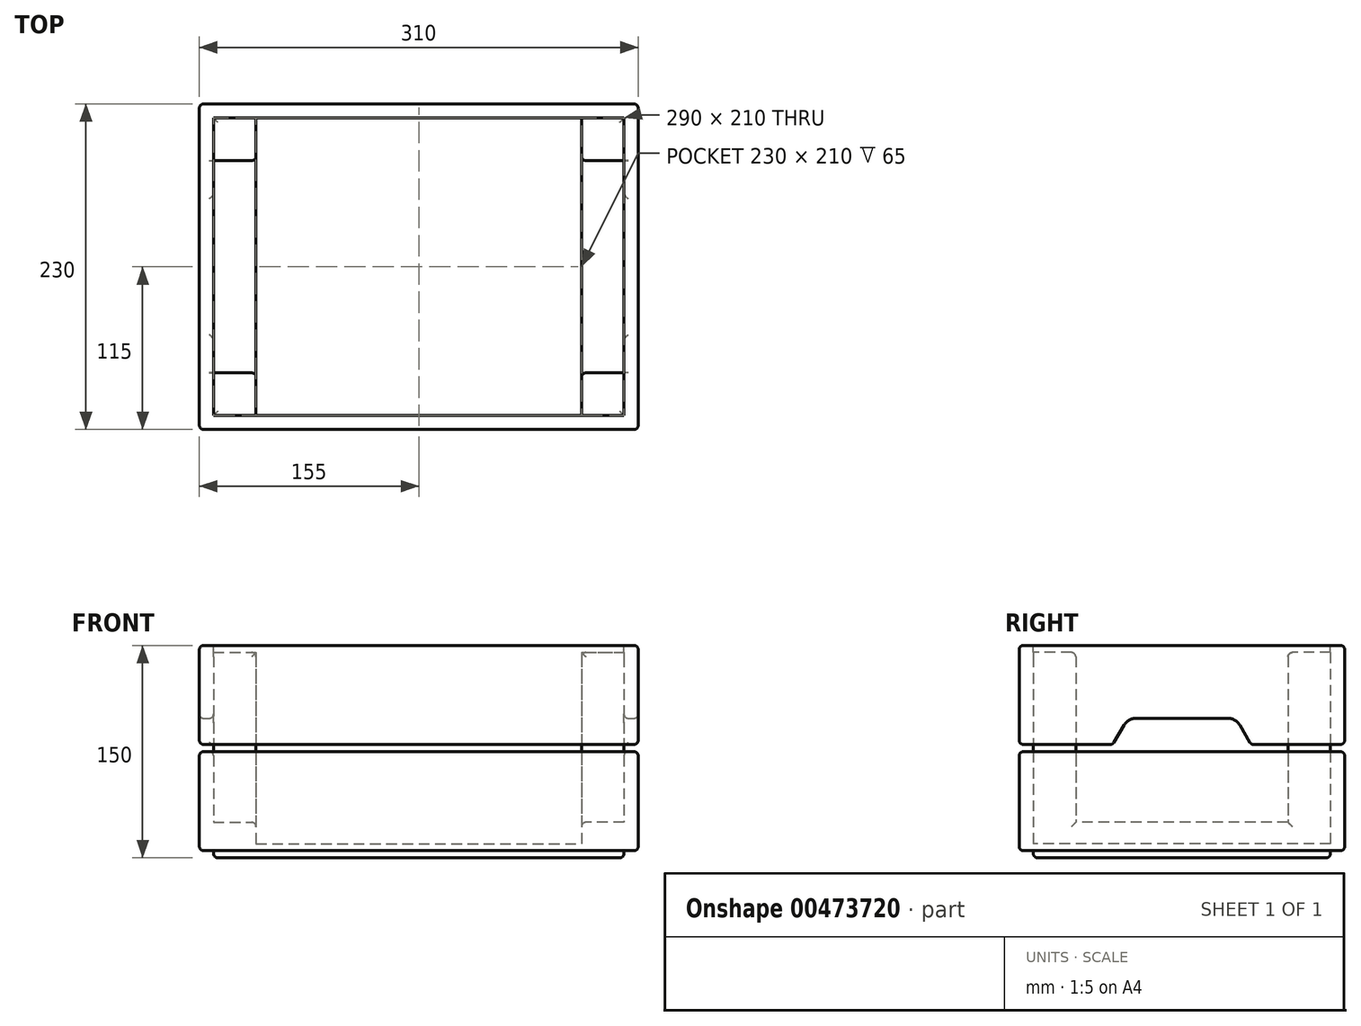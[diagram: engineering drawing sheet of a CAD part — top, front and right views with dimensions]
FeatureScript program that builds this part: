
annotation { "Feature Type Name" : "Feature", "Feature Type Description" : "" }
export const myFeature = defineFeature(function(context is Context, id is Id, definition is map)
    precondition{}
    {
        {
            var Q0;
            Q0=qCreatedBy(makeId("Top.planeOp"),FACE);
            var sketch = newSketch(context, id + "F0", { "sketchPlane" : qUnion([Q0])});
            skLineSegment(sketch, "E0.bottom", {"start": v(-155, 115) * mm, "end": v(155, 115) * mm});
            skLineSegment(sketch, "E0.top", {"start": v(-155, -115) * mm, "end": v(155, -115) * mm});
            skLineSegment(sketch, "E0.left", {"start": v(-155, 115) * mm, "end": v(-155, -115) * mm});
            skLineSegment(sketch, "E0.right", {"start": v(155, 115) * mm, "end": v(155, -115) * mm});
            skSolve(sketch);
        }
        {
            var Q0;
            Q0=makeQuery(id+"F0.imprint","IMPRINT",FACE,{"disambiguationData":[TD([[makeQuery(id+"F0.imprint","IMPRINT",EDGE,{"derivedFrom":sQuery(id+"F0.wireOp",EDGE,"E0.bottom")}),-1.0]])]});
            var sketch = newSketch(context, id + "F1", { "sketchPlane" : qUnion([Q0])});
            skLineSegment(sketch, "E1.0", {"start": v(-145, 105) * mm, "end": v(145, 105) * mm});
            skLineSegment(sketch, "E1.1", {"start": v(-145, 105) * mm, "end": v(-145, -105) * mm});
            skLineSegment(sketch, "E1.2", {"start": v(-145, -105) * mm, "end": v(145, -105) * mm});
            skLineSegment(sketch, "E1.3", {"start": v(145, 105) * mm, "end": v(145, -105) * mm});
            skSolve(sketch);
        }
        {
            var Q0;
            Q0=makeQuery(id+"F0.imprint","IMPRINT",FACE,{"disambiguationData":[TD([[makeQuery(id+"F0.imprint","IMPRINT",EDGE,{"derivedFrom":sQuery(id+"F0.wireOp",EDGE,"E0.bottom")}),-1.0]])]});
            extrude(context, id + "F2", {"entities" : qUnion([Q0]), "depth" : 145 * mm});
        }
        {
            var Q0;
            Q0=makeQuery(id+"F1.imprint","IMPRINT",FACE,{"disambiguationData":[TD([[makeQuery(id+"F1.imprint","IMPRINT",EDGE,{"derivedFrom":sQuery(id+"F1.wireOp",EDGE,"E1.0")}),-1.0]])]});
            extrude(context, id + "F3", {"entities" : qUnion([Q0]), "operationType" : NewBodyOperationType.ADD, "oppositeDirection" : true, "depth" : 5 * mm});
        }
        {
            var Q0;
            Q0=makeQuery(id+"F2.opExtrude","CAP_FACE",FACE,{"disambiguationData":[OSD([sQuery(id+"F0.wireOp",EDGE,"E0.bottom"),sQuery(id+"F0.wireOp",EDGE,"E0.top"),sQuery(id+"F0.wireOp",EDGE,"E0.left"),sQuery(id+"F0.wireOp",EDGE,"E0.right")])],"isStart":false});
            var sketch = newSketch(context, id + "F4", { "sketchPlane" : qUnion([Q0])});
            skLineSegment(sketch, "E2.0", {"start": v(-145, 105) * mm, "end": v(145, 105) * mm});
            skLineSegment(sketch, "E2.1", {"start": v(-145, 105) * mm, "end": v(-145, -105) * mm});
            skLineSegment(sketch, "E2.2", {"start": v(-145, -105) * mm, "end": v(145, -105) * mm});
            skLineSegment(sketch, "E2.3", {"start": v(145, 105) * mm, "end": v(145, -105) * mm});
            skSolve(sketch);
        }
        {
            var Q0;
            Q0=makeQuery(id+"F4.imprint","IMPRINT",FACE,{"disambiguationData":[TD([[makeQuery(id+"F4.imprint","IMPRINT",EDGE,{"derivedFrom":sQuery(id+"F4.wireOp",EDGE,"E2.0")}),-1.0]])]});
            extrude(context, id + "F5", {"entities" : qUnion([Q0]), "operationType" : NewBodyOperationType.REMOVE, "oppositeDirection" : true, "depth" : 140 * mm});
        }
        {
            var Q0;
            Q0=makeQuery(id+"F2.opExtrude","SWEPT_FACE",FACE,{"disambiguationData":[OSD([sQuery(id+"F0.wireOp",EDGE,"E0.right")])]});
            var sketch = newSketch(context, id + "F6", { "sketchPlane" : qUnion([Q0])});
            skLineSegment(sketch, "E3.bottom", {"start": v(-115, 145) * mm, "end": v(115, 145) * mm});
            skLineSegment(sketch, "E3.top", {"start": v(-115, 75) * mm, "end": v(-49, 75) * mm});
            skLineSegment(sketch, "E3.left", {"start": v(-115, 145) * mm, "end": v(-115, 75) * mm});
            skLineSegment(sketch, "E3.right", {"start": v(115, 145) * mm, "end": v(115, 75) * mm});
            skLineSegment(sketch, "E4.bottom", {"start": v(-115, 0) * mm, "end": v(115, 0) * mm});
            skLineSegment(sketch, "E4.top", {"start": v(-115, 70) * mm, "end": v(115, 70) * mm});
            skLineSegment(sketch, "E4.left", {"start": v(-115, 0) * mm, "end": v(-115, 70) * mm});
            skLineSegment(sketch, "E4.right", {"start": v(115, 0) * mm, "end": v(115, 70) * mm});
            skLineSegment(sketch, "E5", {"start": v(-115, 93.5) * mm, "end": v(115, 93.5) * mm, "construction": true});
            skLineSegment(sketch, "E6", {"start": v(49, 145) * mm, "end": v(49, 75) * mm, "construction": true});
            skLineSegment(sketch, "E7", {"start": v(-49, 145) * mm, "end": v(-49, 75) * mm, "construction": true});
            skLineSegment(sketch, "E8", {"start": v(-38, 145) * mm, "end": v(-38, 75) * mm, "construction": true});
            skLineSegment(sketch, "E9", {"start": v(38, 145) * mm, "end": v(38, 75) * mm, "construction": true});
            skLineSegment(sketch, "E10", {"start": v(-49, 75) * mm, "end": v(-40.9, 88.61) * mm});
            skLineSegment(sketch, "E11", {"start": v(-32.31, 93.5) * mm, "end": v(32.31, 93.5) * mm});
            skLineSegment(sketch, "E12", {"start": v(40.9, 88.61) * mm, "end": v(49, 75) * mm});
            skLineSegment(sketch, "E13.trimOffspring", {"start": v(49, 75) * mm, "end": v(115, 75) * mm});
            skPoint(sketch, "E14.visualSharp", {"position": v(-38, 93.5) * mm});
            skArc(sketch, "E14.filletArc", {"start": v(-32.31, 93.5) * mm, "mid": v(-37.26, 92.2) * mm, "end": v(-40.9, 88.61) * mm});
            skPoint(sketch, "E15.visualSharp", {"position": v(38, 93.5) * mm});
            skArc(sketch, "E15.filletArc", {"start": v(40.9, 88.61) * mm, "mid": v(37.26, 92.2) * mm, "end": v(32.31, 93.5) * mm});
            skLineSegment(sketch, "E16", {"start": v(-115, 75) * mm, "end": v(-115, 70) * mm});
            skLineSegment(sketch, "E17", {"start": v(115, 75) * mm, "end": v(115, 70) * mm});
            skSolve(sketch);
        }
        {
            var Q0;
            Q0=makeQuery(id+"F6.imprint","IMPRINT",FACE,{"disambiguationData":[TD([[makeQuery(id+"F6.imprint","IMPRINT",EDGE,{"derivedFrom":sQuery(id+"F6.wireOp",EDGE,"E3.top")}),-1.0]])]});
            extrude(context, id + "F7", {"entities" : qUnion([Q0]), "operationType" : NewBodyOperationType.REMOVE, "endBound" : BoundingType.THROUGH_ALL, "oppositeDirection" : true, "depth" : 25 * mm});
        }
        {
            var Q0;
            Q0=makeQuery(id+"F5.boolean.opBoolean","COPY",FACE,{"derivedFrom":makeQuery(id+"F5.opExtrude","CAP_FACE",FACE,{"disambiguationData":[OSD([sQuery(id+"F4.wireOp",EDGE,"E2.0"),sQuery(id+"F4.wireOp",EDGE,"E2.1"),sQuery(id+"F4.wireOp",EDGE,"E2.2"),sQuery(id+"F4.wireOp",EDGE,"E2.3")])],"isStart":false})});
            var sketch = newSketch(context, id + "F8", { "sketchPlane" : qUnion([Q0])});
            skLineSegment(sketch, "E18.bottom", {"start": v(-145, 105) * mm, "end": v(-115, 105) * mm});
            skLineSegment(sketch, "E18.top", {"start": v(-145, 75) * mm, "end": v(-115, 75) * mm});
            skLineSegment(sketch, "E18.left", {"start": v(-145, 105) * mm, "end": v(-145, 75) * mm});
            skLineSegment(sketch, "E18.right", {"start": v(-115, 105) * mm, "end": v(-115, 75) * mm});
            skLineSegment(sketch, "E19.MirrorCS", {"start": v(-145, -75) * mm, "end": v(-115, -75) * mm});
            skLineSegment(sketch, "E20.MirrorCS", {"start": v(-145, -105) * mm, "end": v(-145, -75) * mm});
            skLineSegment(sketch, "E21.MirrorCS", {"start": v(-145, -105) * mm, "end": v(-115, -105) * mm});
            skLineSegment(sketch, "E22.MirrorCS", {"start": v(-115, -105) * mm, "end": v(-115, -75) * mm});
            skLineSegment(sketch, "E23.MirrorCS", {"start": v(145, 75) * mm, "end": v(115, 75) * mm});
            skLineSegment(sketch, "E24.MirrorCS", {"start": v(145, 105) * mm, "end": v(145, 75) * mm});
            skLineSegment(sketch, "E25.MirrorCS", {"start": v(145, 105) * mm, "end": v(115, 105) * mm});
            skLineSegment(sketch, "E26.MirrorCS", {"start": v(115, 105) * mm, "end": v(115, 75) * mm});
            skLineSegment(sketch, "E27.MirrorCS", {"start": v(145, -75) * mm, "end": v(115, -75) * mm});
            skLineSegment(sketch, "E28.MirrorCS", {"start": v(145, -105) * mm, "end": v(145, -75) * mm});
            skLineSegment(sketch, "E29.MirrorCS", {"start": v(145, -105) * mm, "end": v(115, -105) * mm});
            skLineSegment(sketch, "E30.MirrorCS", {"start": v(115, -105) * mm, "end": v(115, -75) * mm});
            skSolve(sketch);
        }
        {
            var Q0;
            Q0=makeQuery(id+"F8.imprint","IMPRINT",FACE,{"disambiguationData":[TD([[makeQuery(id+"F8.imprint","IMPRINT",EDGE,{"derivedFrom":sQuery(id+"F8.wireOp",EDGE,"E18.bottom")}),-1.0]])]});
            var Q1;
            Q1=makeQuery(id+"F8.imprint","IMPRINT",FACE,{"disambiguationData":[TD([[makeQuery(id+"F8.imprint","IMPRINT",EDGE,{"derivedFrom":sQuery(id+"F8.wireOp",EDGE,"E23.MirrorCS")}),-1.0]])]});
            var Q2;
            Q2=makeQuery(id+"F8.imprint","IMPRINT",FACE,{"disambiguationData":[TD([[makeQuery(id+"F8.imprint","IMPRINT",EDGE,{"derivedFrom":sQuery(id+"F8.wireOp",EDGE,"E27.MirrorCS")}),1.0]])]});
            var Q3;
            Q3=makeQuery(id+"F8.imprint","IMPRINT",FACE,{"disambiguationData":[TD([[makeQuery(id+"F8.imprint","IMPRINT",EDGE,{"derivedFrom":sQuery(id+"F8.wireOp",EDGE,"E19.MirrorCS")}),-1.0]])]});
            var Q4;
            Q4=makeQuery(id+"F2.opExtrude","CAP_FACE",FACE,{"disambiguationData":[OSD([sQuery(id+"F0.wireOp",EDGE,"E0.bottom"),sQuery(id+"F0.wireOp",EDGE,"E0.top"),sQuery(id+"F0.wireOp",EDGE,"E0.left"),sQuery(id+"F0.wireOp",EDGE,"E0.right")])],"isStart":false});
            extrude(context, id + "F9", {"entities" : qUnion([Q0, Q1, Q2, Q3]), "operationType" : NewBodyOperationType.ADD, "endBoundEntityFace" : qUnion([Q4]), "depth" : 135 * mm, "hasSecondDirection" : true, "secondDirectionOppositeDirection" : false, "secondDirectionDepth" : 15 * mm});
        }
        {
            var Q0;
            Q0=makeQuery(id+"F5.boolean.opBoolean","COPY",FACE,{"derivedFrom":makeQuery(id+"F5.opExtrude","CAP_FACE",FACE,{"disambiguationData":[OSD([sQuery(id+"F4.wireOp",EDGE,"E2.0"),sQuery(id+"F4.wireOp",EDGE,"E2.1"),sQuery(id+"F4.wireOp",EDGE,"E2.2"),sQuery(id+"F4.wireOp",EDGE,"E2.3")])],"isStart":false})});
            var sketch = newSketch(context, id + "F10", { "sketchPlane" : qUnion([Q0])});
            skLineSegment(sketch, "E31.0", {"start": v(115, -105) * mm, "end": v(115, -75) * mm});
            skLineSegment(sketch, "E32.bottom", {"start": v(145, 105) * mm, "end": v(115, 105) * mm});
            skLineSegment(sketch, "E32.top", {"start": v(145, -105) * mm, "end": v(115, -105) * mm});
            skLineSegment(sketch, "E32.left", {"start": v(145, 105) * mm, "end": v(145, -105) * mm});
            skLineSegment(sketch, "E32.right", {"start": v(115, 105) * mm, "end": v(115, -105) * mm});
            skLineSegment(sketch, "E33.MirrorCS", {"start": v(-115, 105) * mm, "end": v(-115, -105) * mm});
            skLineSegment(sketch, "E34.MirrorCS", {"start": v(-145, -105) * mm, "end": v(-115, -105) * mm});
            skLineSegment(sketch, "E35.MirrorCS", {"start": v(-145, 105) * mm, "end": v(-145, -105) * mm});
            skLineSegment(sketch, "E36.MirrorCS", {"start": v(-145, 105) * mm, "end": v(-115, 105) * mm});
            skSolve(sketch);
        }
        {
            var Q0;
            {var subQ1=sQuery(id+"F10.wireOp",EDGE,"E32.bottom");Q0=makeQuery(id+"F10.imprint","IMPRINT",FACE,{"disambiguationData":[TD([[makeQuery(id+"F10.imprint","IMPRINT",EDGE,{"derivedFrom":subQ1}),-1.0]])]});}
            var Q1;
            Q1=makeQuery(id+"F10.imprint","IMPRINT",FACE,{"disambiguationData":[TD([[makeQuery(id+"F10.imprint","IMPRINT",EDGE,{"derivedFrom":sQuery(id+"F10.wireOp",EDGE,"E33.MirrorCS")}),-1.0]])]});
            extrude(context, id + "F11", {"entities" : qUnion([Q0, Q1]), "operationType" : NewBodyOperationType.ADD, "depth" : 15 * mm});
        }
        {
            var Q0;
            {var subQ1=sQuery(id+"F0.wireOp",EDGE,"E0.right");Q0=makeQuery(id+"F7.boolean.opBoolean","SPLIT",FACE,{"disambiguationData":[TD([makeQuery(id+"F7.opExtrude","SWEPT_FACE",FACE,{"disambiguationData":[OSD([sQuery(id+"F6.wireOp",EDGE,"E4.top")])]})])],"derivedFrom":makeQuery(id+"F2.opExtrude","SWEPT_FACE",FACE,{"disambiguationData":[OSD([subQ1])]})});}
            var Q1;
            {var subQ1=sQuery(id+"F0.wireOp",EDGE,"E0.right");Q1=makeQuery(id+"F7.boolean.opBoolean","SPLIT",FACE,{"disambiguationData":[TD([makeQuery(id+"F7.opExtrude","SWEPT_FACE",FACE,{"disambiguationData":[OSD([sQuery(id+"F6.wireOp",EDGE,"E3.top")])]})])],"derivedFrom":makeQuery(id+"F2.opExtrude","SWEPT_FACE",FACE,{"disambiguationData":[OSD([subQ1])]})});}
            var Q2;
            {var subQ2=sQuery(id+"F0.wireOp",EDGE,"E0.top");Q2=makeQuery(id+"F7.boolean.opBoolean","SPLIT",FACE,{"disambiguationData":[TD([makeQuery(id+"F7.opExtrude","SWEPT_FACE",FACE,{"disambiguationData":[OSD([sQuery(id+"F6.wireOp",EDGE,"E4.top")])]})])],"derivedFrom":makeQuery(id+"F2.opExtrude","SWEPT_FACE",FACE,{"disambiguationData":[OSD([subQ2])]})});}
            var Q3;
            {var subQ2=sQuery(id+"F0.wireOp",EDGE,"E0.top");Q3=makeQuery(id+"F7.boolean.opBoolean","SPLIT",FACE,{"disambiguationData":[TD([makeQuery(id+"F7.opExtrude","SWEPT_FACE",FACE,{"disambiguationData":[OSD([sQuery(id+"F6.wireOp",EDGE,"E3.top")])]})])],"derivedFrom":makeQuery(id+"F2.opExtrude","SWEPT_FACE",FACE,{"disambiguationData":[OSD([subQ2])]})});}
            var Q4;
            {var subQ1=sQuery(id+"F0.wireOp",EDGE,"E0.left");Q4=makeQuery(id+"F7.boolean.opBoolean","SPLIT",FACE,{"disambiguationData":[TD([makeQuery(id+"F7.opExtrude","SWEPT_FACE",FACE,{"disambiguationData":[OSD([sQuery(id+"F6.wireOp",EDGE,"E3.top")])]})])],"derivedFrom":makeQuery(id+"F2.opExtrude","SWEPT_FACE",FACE,{"disambiguationData":[OSD([subQ1])]})});}
            var Q5;
            {var subQ1=sQuery(id+"F0.wireOp",EDGE,"E0.left");Q5=makeQuery(id+"F7.boolean.opBoolean","SPLIT",FACE,{"disambiguationData":[TD([makeQuery(id+"F7.opExtrude","SWEPT_FACE",FACE,{"disambiguationData":[OSD([sQuery(id+"F6.wireOp",EDGE,"E4.top")])]})])],"derivedFrom":makeQuery(id+"F2.opExtrude","SWEPT_FACE",FACE,{"disambiguationData":[OSD([subQ1])]})});}
            var Q6;
            {var subQ2=sQuery(id+"F0.wireOp",EDGE,"E0.bottom");Q6=makeQuery(id+"F7.boolean.opBoolean","SPLIT",FACE,{"disambiguationData":[TD([makeQuery(id+"F7.opExtrude","SWEPT_FACE",FACE,{"disambiguationData":[OSD([sQuery(id+"F6.wireOp",EDGE,"E4.top")])]})])],"derivedFrom":makeQuery(id+"F2.opExtrude","SWEPT_FACE",FACE,{"disambiguationData":[OSD([subQ2])]})});}
            var Q7;
            {var subQ2=sQuery(id+"F0.wireOp",EDGE,"E0.bottom");Q7=makeQuery(id+"F7.boolean.opBoolean","SPLIT",FACE,{"disambiguationData":[TD([makeQuery(id+"F7.opExtrude","SWEPT_FACE",FACE,{"disambiguationData":[OSD([sQuery(id+"F6.wireOp",EDGE,"E13.trimOffspring")])]})])],"derivedFrom":makeQuery(id+"F2.opExtrude","SWEPT_FACE",FACE,{"disambiguationData":[OSD([subQ2])]})});}
            var Q8;
            Q8=makeQuery(id+"F5.boolean.opBoolean","COPY",EDGE,{"derivedFrom":makeQuery(id+"F5.opExtrude","CAP_EDGE",EDGE,{"disambiguationData":[OSD([sQuery(id+"F4.wireOp",EDGE,"E2.0")])],"isStart":true})});
            var Q9;
            Q9=makeQuery(id+"F5.boolean.opBoolean","COPY",EDGE,{"derivedFrom":makeQuery(id+"F5.opExtrude","CAP_EDGE",EDGE,{"disambiguationData":[OSD([sQuery(id+"F4.wireOp",EDGE,"E2.3")])],"isStart":true})});
            var Q10;
            Q10=makeQuery(id+"F5.boolean.opBoolean","COPY",EDGE,{"derivedFrom":makeQuery(id+"F5.opExtrude","CAP_EDGE",EDGE,{"disambiguationData":[OSD([sQuery(id+"F4.wireOp",EDGE,"E2.2")])],"isStart":true})});
            var Q11;
            Q11=makeQuery(id+"F5.boolean.opBoolean","COPY",EDGE,{"derivedFrom":makeQuery(id+"F5.opExtrude","CAP_EDGE",EDGE,{"disambiguationData":[OSD([sQuery(id+"F4.wireOp",EDGE,"E2.1")])],"isStart":true})});
            var Q12;
            Q12=makeQuery(id+"F9.opExtrude","CAP_EDGE",EDGE,{"disambiguationData":[OSD([sQuery(id+"F8.wireOp",EDGE,"E19.MirrorCS")])],"isStart":false});
            var Q13;
            Q13=makeQuery(id+"F9.opExtrude","CAP_EDGE",EDGE,{"disambiguationData":[OSD([sQuery(id+"F8.wireOp",EDGE,"E22.MirrorCS")])],"isStart":false});
            var Q14;
            Q14=makeQuery(id+"F9.opExtrude","SWEPT_EDGE",EDGE,{"disambiguationData":[OSD([sQuery(id+"F8.wireOp",EDGE,"E19.MirrorCS"),sQuery(id+"F8.wireOp",EDGE,"E22.MirrorCS")])]});
            var Q15;
            Q15=makeQuery(id+"F9.opExtrude","CAP_EDGE",EDGE,{"disambiguationData":[OSD([sQuery(id+"F8.wireOp",EDGE,"E30.MirrorCS")])],"isStart":false});
            var Q16;
            Q16=makeQuery(id+"F9.opExtrude","SWEPT_EDGE",EDGE,{"disambiguationData":[OSD([sQuery(id+"F8.wireOp",EDGE,"E27.MirrorCS"),sQuery(id+"F8.wireOp",EDGE,"E30.MirrorCS")])]});
            var Q17;
            Q17=makeQuery(id+"F9.opExtrude","CAP_EDGE",EDGE,{"disambiguationData":[OSD([sQuery(id+"F8.wireOp",EDGE,"E27.MirrorCS")])],"isStart":false});
            var Q18;
            Q18=makeQuery(id+"F11.opExtrude","CAP_EDGE",EDGE,{"disambiguationData":[OSD([sQuery(id+"F10.wireOp",EDGE,"E32.right")])],"isStart":false});
            var Q19;
            Q19=makeQuery(id+"F9.opExtrude","SWEPT_EDGE",EDGE,{"disambiguationData":[OSD([sQuery(id+"F8.wireOp",EDGE,"E23.MirrorCS"),sQuery(id+"F8.wireOp",EDGE,"E26.MirrorCS")])]});
            var Q20;
            Q20=makeQuery(id+"F9.opExtrude","CAP_EDGE",EDGE,{"disambiguationData":[OSD([sQuery(id+"F8.wireOp",EDGE,"E23.MirrorCS")])],"isStart":false});
            var Q21;
            Q21=makeQuery(id+"F11.opExtrude","CAP_EDGE",EDGE,{"disambiguationData":[OSD([sQuery(id+"F10.wireOp",EDGE,"E33.MirrorCS")])],"isStart":false});
            var Q22;
            Q22=makeQuery(id+"F9.opExtrude","SWEPT_EDGE",EDGE,{"disambiguationData":[OSD([sQuery(id+"F8.wireOp",EDGE,"E18.top"),sQuery(id+"F8.wireOp",EDGE,"E18.right")])]});
            var Q23;
            Q23=makeQuery(id+"F9.opExtrude","CAP_EDGE",EDGE,{"disambiguationData":[OSD([sQuery(id+"F8.wireOp",EDGE,"E18.top")])],"isStart":false});
            var Q24;
            {var subQ0=makeQuery(id+"F5.boolean.opBoolean","COPY",FACE,{"derivedFrom":makeQuery(id+"F5.opExtrude","SWEPT_FACE",FACE,{"disambiguationData":[OSD([sQuery(id+"F4.wireOp",EDGE,"E2.3")])]})});var subQ1=makeQuery(id+"F7.opExtrude","SWEPT_FACE",FACE,{"disambiguationData":[OSD([sQuery(id+"F6.wireOp",EDGE,"E4.top")])]});Q24=makeQuery(id+"F9.boolean.opBoolean","SPLIT",EDGE,{"disambiguationData":[topologyDisambiguationEdgeConnected([subQ0])],"derivedFrom":makeQuery(id+"F7.boolean.opBoolean","INTERSECT",EDGE,{"derivedFrom":[subQ0,subQ1]})});}
            var Q25;
            {var subQ0=makeQuery(id+"F5.boolean.opBoolean","COPY",FACE,{"derivedFrom":makeQuery(id+"F5.opExtrude","SWEPT_FACE",FACE,{"disambiguationData":[OSD([sQuery(id+"F4.wireOp",EDGE,"E2.1")])]})});var subQ1=makeQuery(id+"F7.opExtrude","SWEPT_FACE",FACE,{"disambiguationData":[OSD([sQuery(id+"F6.wireOp",EDGE,"E4.top")])]});Q25=makeQuery(id+"F9.boolean.opBoolean","SPLIT",EDGE,{"disambiguationData":[topologyDisambiguationEdgeConnected([subQ0])],"derivedFrom":makeQuery(id+"F7.boolean.opBoolean","INTERSECT",EDGE,{"derivedFrom":[subQ0,subQ1]})});}
            var Q26;
            Q26=makeQuery(id+"F7.boolean.opBoolean","INTERSECT",EDGE,{"derivedFrom":[makeQuery(id+"F5.boolean.opBoolean","COPY",FACE,{"derivedFrom":makeQuery(id+"F5.opExtrude","SWEPT_FACE",FACE,{"disambiguationData":[OSD([sQuery(id+"F4.wireOp",EDGE,"E2.1")])]})}),makeQuery(id+"F7.opExtrude","SWEPT_FACE",FACE,{"disambiguationData":[OSD([sQuery(id+"F6.wireOp",EDGE,"E15.filletArc")])]})]});
            var Q27;
            Q27=makeQuery(id+"F7.boolean.opBoolean","INTERSECT",EDGE,{"derivedFrom":[makeQuery(id+"F5.boolean.opBoolean","COPY",FACE,{"derivedFrom":makeQuery(id+"F5.opExtrude","SWEPT_FACE",FACE,{"disambiguationData":[OSD([sQuery(id+"F4.wireOp",EDGE,"E2.3")])]})}),makeQuery(id+"F7.opExtrude","SWEPT_FACE",FACE,{"disambiguationData":[OSD([sQuery(id+"F6.wireOp",EDGE,"E15.filletArc")])]})]});
            var Q28;
            {var subQ0=sQuery(id+"F6.wireOp",EDGE,"E3.top");var subQ1=sQuery(id+"F6.wireOp",EDGE,"E10");Q28=makeQuery(id+"F7.boolean.opBoolean","COPY",EDGE,{"disambiguationData":[TD([makeQuery(id+"F2.opExtrude","SWEPT_FACE",FACE,{"disambiguationData":[OSD([sQuery(id+"F0.wireOp",EDGE,"E0.right")])]})])],"derivedFrom":makeQuery(id+"F7.opExtrude","SWEPT_EDGE",EDGE,{"disambiguationData":[OSD([subQ0,subQ1])]})});}
            var Q29;
            {var subQ0=sQuery(id+"F6.wireOp",EDGE,"E12");var subQ1=sQuery(id+"F6.wireOp",EDGE,"E13.trimOffspring");Q29=makeQuery(id+"F7.boolean.opBoolean","COPY",EDGE,{"disambiguationData":[TD([makeQuery(id+"F2.opExtrude","SWEPT_FACE",FACE,{"disambiguationData":[OSD([sQuery(id+"F0.wireOp",EDGE,"E0.right")])]})])],"derivedFrom":makeQuery(id+"F7.opExtrude","SWEPT_EDGE",EDGE,{"disambiguationData":[OSD([subQ0,subQ1])]})});}
            var Q30;
            Q30=makeQuery(id+"F3.opExtrude","CAP_FACE",FACE,{"disambiguationData":[OSD([sQuery(id+"F1.wireOp",EDGE,"E1.0"),sQuery(id+"F1.wireOp",EDGE,"E1.1"),sQuery(id+"F1.wireOp",EDGE,"E1.2"),sQuery(id+"F1.wireOp",EDGE,"E1.3")])],"isStart":false});
            var Q31;
            {var subQ0=sQuery(id+"F6.wireOp",EDGE,"E3.top");var subQ1=sQuery(id+"F6.wireOp",EDGE,"E10");Q31=makeQuery(id+"F7.boolean.opBoolean","COPY",EDGE,{"disambiguationData":[TD([makeQuery(id+"F2.opExtrude","SWEPT_FACE",FACE,{"disambiguationData":[OSD([sQuery(id+"F0.wireOp",EDGE,"E0.left")])]})])],"derivedFrom":makeQuery(id+"F7.opExtrude","SWEPT_EDGE",EDGE,{"disambiguationData":[OSD([subQ0,subQ1])]})});}
            var Q32;
            {var subQ0=sQuery(id+"F6.wireOp",EDGE,"E12");var subQ1=sQuery(id+"F6.wireOp",EDGE,"E13.trimOffspring");Q32=makeQuery(id+"F7.boolean.opBoolean","COPY",EDGE,{"disambiguationData":[TD([makeQuery(id+"F2.opExtrude","SWEPT_FACE",FACE,{"disambiguationData":[OSD([sQuery(id+"F0.wireOp",EDGE,"E0.left")])]})])],"derivedFrom":makeQuery(id+"F7.opExtrude","SWEPT_EDGE",EDGE,{"disambiguationData":[OSD([subQ0,subQ1])]})});}
            fillet(context, id + "F12", {"entities" : qUnion([Q0, Q1, Q2, Q3, Q4, Q5, Q6, Q7, Q8, Q9, Q10, Q11, Q12, Q13, Q14, Q15, Q16, Q17, Q18, Q19, Q20, Q21, Q22, Q23, Q24, Q25, Q26, Q27, Q28, Q29, Q30, Q31, Q32]), "radius" : 3 * mm, "tangentPropagation" : true, "allowEdgeOverflow" : false});
        }
    });
